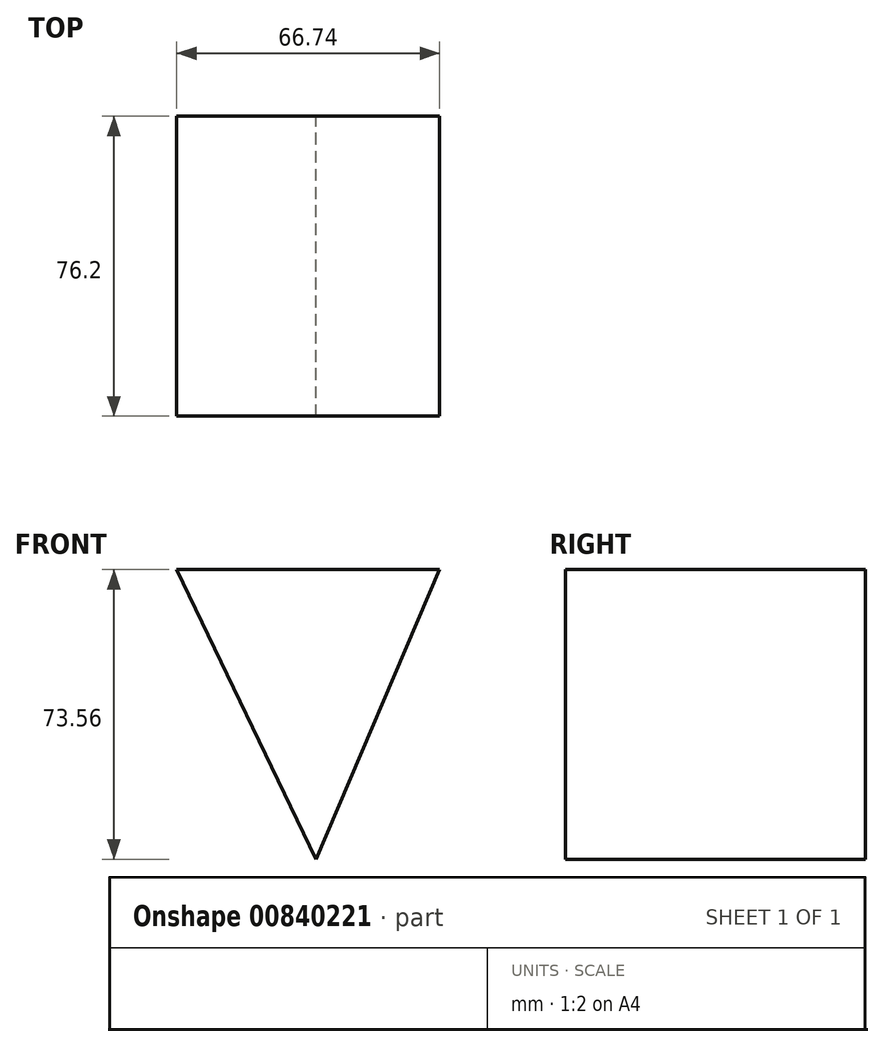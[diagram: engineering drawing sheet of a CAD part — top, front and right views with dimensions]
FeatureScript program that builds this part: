
annotation { "Feature Type Name" : "Feature", "Feature Type Description" : "" }
export const myFeature = defineFeature(function(context is Context, id is Id, definition is map)
    precondition{}
    {
        {
            var Q0;
            Q0=qCreatedBy(makeId("Front.planeOp"),FACE);
            var sketch = newSketch(context, id + "F0", { "sketchPlane" : qUnion([Q0])});
            skLineSegment(sketch, "E0", {"start": v(-23.32, 31.62) * mm, "end": v(43.42, 31.62) * mm});
            skLineSegment(sketch, "E1", {"start": v(43.42, 31.62) * mm, "end": v(12.08, -41.94) * mm});
            skLineSegment(sketch, "E2", {"start": v(12.08, -41.94) * mm, "end": v(-23.32, 31.62) * mm});
            skSolve(sketch);
        }
        {
            var Q0;
            Q0 = qSketchRegion(id + "F0", true);
            extrude(context, id + "F1", {"entities" : qUnion([Q0]), "depth" : 76.2 * mm, "offsetDistance" : 25.4 * mm});
        }
    });
